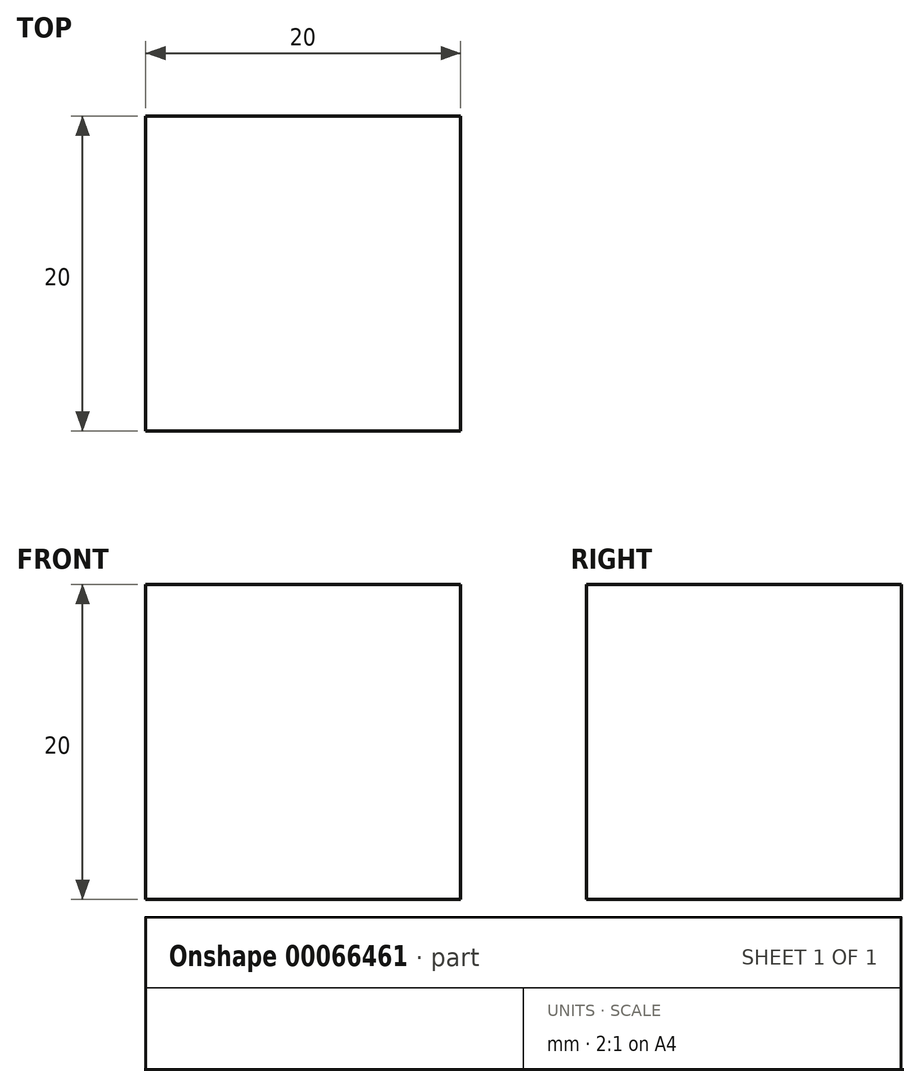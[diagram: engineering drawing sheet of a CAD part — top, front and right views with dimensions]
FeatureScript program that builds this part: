
annotation { "Feature Type Name" : "Feature", "Feature Type Description" : "" }
export const myFeature = defineFeature(function(context is Context, id is Id, definition is map)
    precondition{}
    {
        {
            var Q0;
            Q0=qCreatedBy(makeId("Front.planeOp"),FACE);
            var sketch = newSketch(context, id + "F0", { "sketchPlane" : qUnion([Q0])});
            skLineSegment(sketch, "E0.rect.bottom", {"start": v(10, 10) * mm, "end": v(-10, 10) * mm});
            skLineSegment(sketch, "E0.rect.top", {"start": v(10, -10) * mm, "end": v(-10, -10) * mm});
            skLineSegment(sketch, "E0.rect.left", {"start": v(10, 10) * mm, "end": v(10, -10) * mm});
            skLineSegment(sketch, "E0.rect.right", {"start": v(-10, 10) * mm, "end": v(-10, -10) * mm});
            skPoint(sketch, "E0.rect.middle", {"position": v(0, 0) * mm});
            skSolve(sketch);
        }
        {
            var Q0;
            Q0 = qSketchRegion(id + "F0", true);
            extrude(context, id + "F1", {"entities" : qUnion([Q0]), "endBound" : BoundingType.SYMMETRIC, "depth" : 20 * mm});
        }
    });
